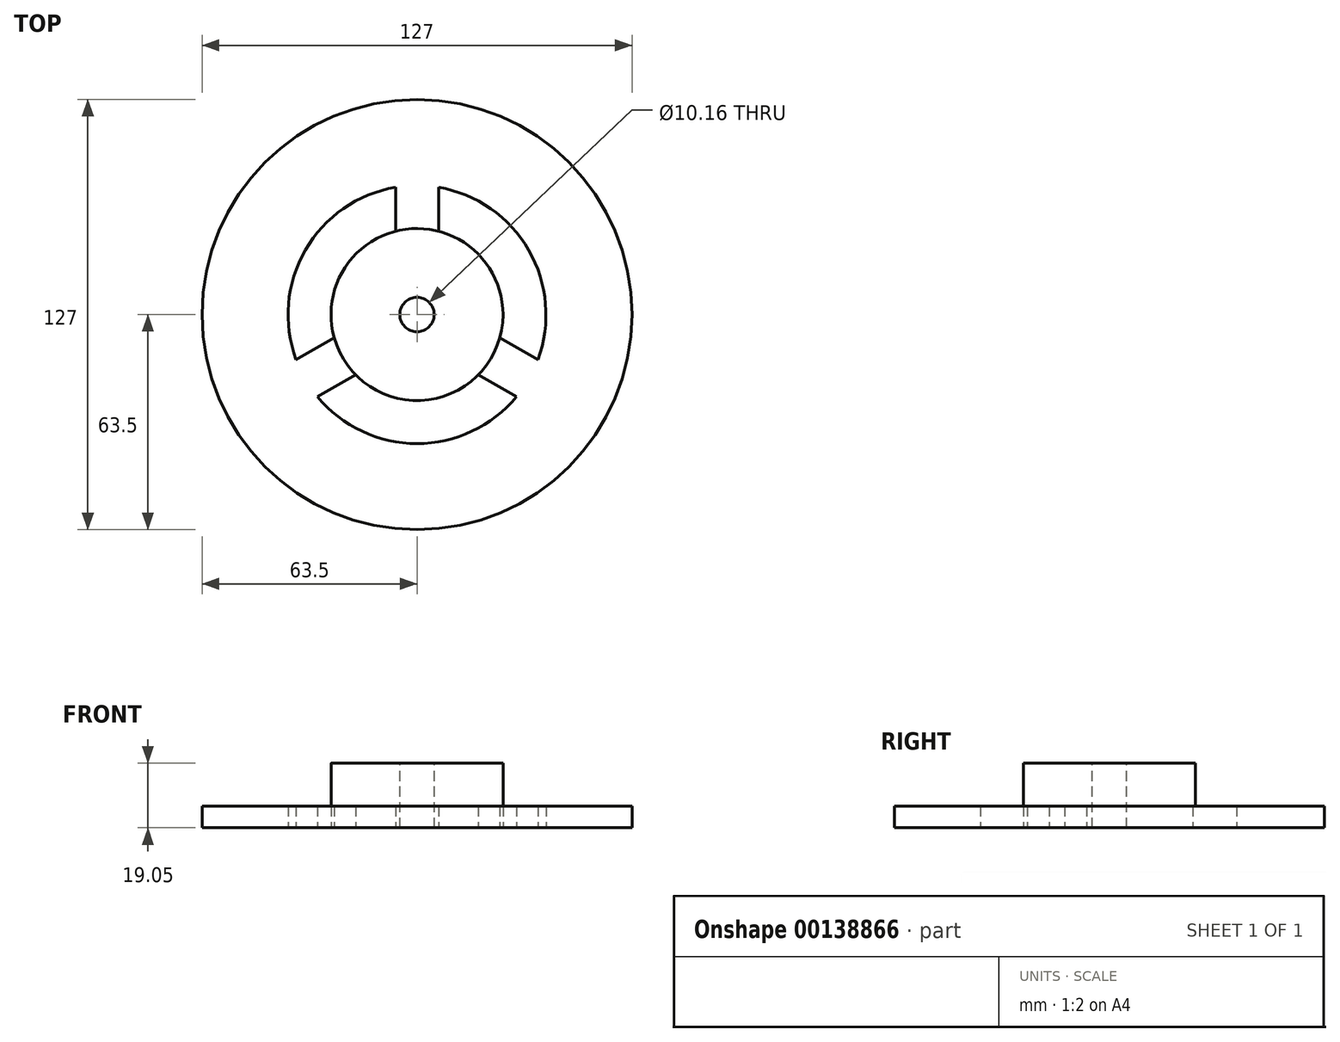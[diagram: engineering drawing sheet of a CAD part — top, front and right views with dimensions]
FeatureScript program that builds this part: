
annotation { "Feature Type Name" : "Feature", "Feature Type Description" : "" }
export const myFeature = defineFeature(function(context is Context, id is Id, definition is map)
    precondition{}
    {
        {
            var Q0;
            Q0=qCreatedBy(makeId("Top.planeOp"),FACE);
            var sketch = newSketch(context, id + "F0", { "sketchPlane" : qUnion([Q0])});
            skCircle(sketch, "E0", {"center": v(0, 0) * mm, "radius": 63.5 * mm});
            skCircle(sketch, "E1", {"center": v(0, 0) * mm, "radius": 38.1 * mm});
            skSolve(sketch);
        }
        {
            var Q0;
            Q0=qSketchRegion(id+"F0",true);
            extrude(context, id + "F1", {"entities" : qUnion([Q0]), "depth" : 6.35 * mm});
        }
        {
            var Q0;
            Q0=qCreatedBy(makeId("Top.planeOp"),FACE);
            var sketch = newSketch(context, id + "F2", { "sketchPlane" : qUnion([Q0])});
            skCircle(sketch, "E2.0", {"center": v(0, 0) * mm, "radius": 50.8 * mm});
            skCircle(sketch, "E2.1", {"center": v(0, 0) * mm, "radius": 25.4 * mm});
            skLineSegment(sketch, "E3.1.0", {"start": v(-6.35, 50.4) * mm, "end": v(-6.35, 24.6) * mm});
            skLineSegment(sketch, "E3.1.1", {"start": v(6.35, 50.4) * mm, "end": v(6.35, 24.6) * mm});
            skLineSegment(sketch, "E4.1.0", {"start": v(-40.47, -30.7) * mm, "end": v(-18.12, -17.8) * mm});
            skLineSegment(sketch, "E4.1.1", {"start": v(-46.82, -19.7) * mm, "end": v(-24.47, -6.8) * mm});
            skLineSegment(sketch, "E4.2.0", {"start": v(46.82, -19.7) * mm, "end": v(24.47, -6.8) * mm});
            skLineSegment(sketch, "E4.2.1", {"start": v(40.47, -30.7) * mm, "end": v(18.12, -17.8) * mm});
            skSolve(sketch);
        }
        {
            var Q0;
            Q0=qCreatedBy(makeId("Top.planeOp"),FACE);
            var sketch = newSketch(context, id + "F3", { "sketchPlane" : qUnion([Q0])});
            skCircle(sketch, "E5", {"center": v(0, 0) * mm, "radius": 25.4 * mm});
            skSolve(sketch);
        }
        {
            var Q0;
            {var subQ0=sQuery(id+"F2.wireOp",EDGE,"E2.1");var subQ4=makeQuery(id+"F2.imprint","INTERSECT",VERTEX,{"derivedFrom":[subQ0,sQuery(id+"F2.wireOp",EDGE,"E3.1.0")]});Q0=makeQuery(id+"F2.imprint","IMPRINT",FACE,{"disambiguationData":[TD([[makeQuery(id+"F2.imprint","IMPRINT",EDGE,{"disambiguationData":[TD([[subQ4,1.0]])],"derivedFrom":subQ0}),1.0]])]});}
            var Q1;
            {var subQ0=sQuery(id+"F2.wireOp",EDGE,"E4.1.0");Q1=makeQuery(id+"F2.imprint","IMPRINT",FACE,{"disambiguationData":[TD([[makeQuery(id+"F2.imprint","IMPRINT",EDGE,{"derivedFrom":subQ0}),1.0]])]});}
            var Q2;
            {var subQ0=sQuery(id+"F2.wireOp",EDGE,"E3.1.0");Q2=makeQuery(id+"F2.imprint","IMPRINT",FACE,{"disambiguationData":[TD([[makeQuery(id+"F2.imprint","IMPRINT",EDGE,{"derivedFrom":subQ0}),1.0]])]});}
            var Q3;
            {var subQ0=sQuery(id+"F2.wireOp",EDGE,"E4.2.0");Q3=makeQuery(id+"F2.imprint","IMPRINT",FACE,{"disambiguationData":[TD([[makeQuery(id+"F2.imprint","IMPRINT",EDGE,{"derivedFrom":subQ0}),1.0]])]});}
            var Q4;
            Q4=makeQuery(id+"F1.opExtrude","CAP_FACE",FACE,{"disambiguationData":[OSD([sQuery(id+"F0.wireOp",EDGE,"E0"),sQuery(id+"F0.wireOp",EDGE,"E1")])],"isStart":false});
            extrude(context, id + "F4", {"entities" : qUnion([Q0, Q1, Q2, Q3]), "operationType" : NewBodyOperationType.ADD, "endBound" : BoundingType.UP_TO_SURFACE, "endBoundEntityFace" : qUnion([Q4]), "depth" : 25.4 * mm});
        }
        {
            var Q0;
            {var subQ0=sQuery(id+"F0.wireOp",EDGE,"E1");var subQ1=sQuery(id+"F0.wireOp",EDGE,"E0");Q0=makeQuery(id+"F4.boolean.opBoolean","MERGE",FACE,{"derivedFrom":[makeQuery(id+"F1.opExtrude","CAP_FACE",FACE,{"disambiguationData":[OSD([subQ1,subQ0])],"isStart":false}),makeQuery(id+"F4.opExtrude","CAP_FACE",FACE,{"disambiguationData":[OSD([subQ1,subQ0])],"isStart":false})]});}
            var sketch = newSketch(context, id + "F5", { "sketchPlane" : qUnion([Q0])});
            skCircle(sketch, "E6.0", {"center": v(0, 0) * mm, "radius": 25.4 * mm});
            skSolve(sketch);
        }
        {
            var Q0;
            Q0=qSketchRegion(id+"F5",true);
            extrude(context, id + "F6", {"entities" : qUnion([Q0]), "operationType" : NewBodyOperationType.ADD, "depth" : 12.7 * mm});
        }
        {
            var Q0;
            Q0=makeQuery(id+"F6.opExtrude","CAP_FACE",FACE,{"disambiguationData":[OSD([sQuery(id+"F5.wireOp",EDGE,"E6.0")])],"isStart":false});
            var sketch = newSketch(context, id + "F7", { "sketchPlane" : qUnion([Q0])});
            skCircle(sketch, "E7", {"center": v(0, 0) * mm, "radius": 5.08 * mm});
            skSolve(sketch);
        }
        {
            var Q0;
            Q0 = qSketchRegion(id + "F7", true);
            var Q1;
            Q1=makeQuery(id+"F4.boolean.opBoolean","MERGE",FACE,{"derivedFrom":[makeQuery(id+"F1.opExtrude","CAP_FACE",FACE,{"disambiguationData":[OSD([sQuery(id+"F0.wireOp",EDGE,"E0"),sQuery(id+"F0.wireOp",EDGE,"E1")])],"isStart":true}),makeQuery(id+"F4.opExtrude","CAP_FACE",FACE,{"disambiguationData":[OSD([sQuery(id+"F2.wireOp",EDGE,"E2.0"),sQuery(id+"F2.wireOp",EDGE,"E2.1"),sQuery(id+"F2.wireOp",EDGE,"E3.1.0"),sQuery(id+"F2.wireOp",EDGE,"E3.1.1"),sQuery(id+"F2.wireOp",EDGE,"E4.1.0"),sQuery(id+"F2.wireOp",EDGE,"E4.1.1"),sQuery(id+"F2.wireOp",EDGE,"E4.2.0"),sQuery(id+"F2.wireOp",EDGE,"E4.2.1")])],"isStart":true})]});
            extrude(context, id + "F8", {"entities" : qUnion([Q0]), "operationType" : NewBodyOperationType.REMOVE, "endBound" : BoundingType.UP_TO_SURFACE, "oppositeDirection" : true, "endBoundEntityFace" : qUnion([Q1]), "depth" : 25.4 * mm});
        }
    });
